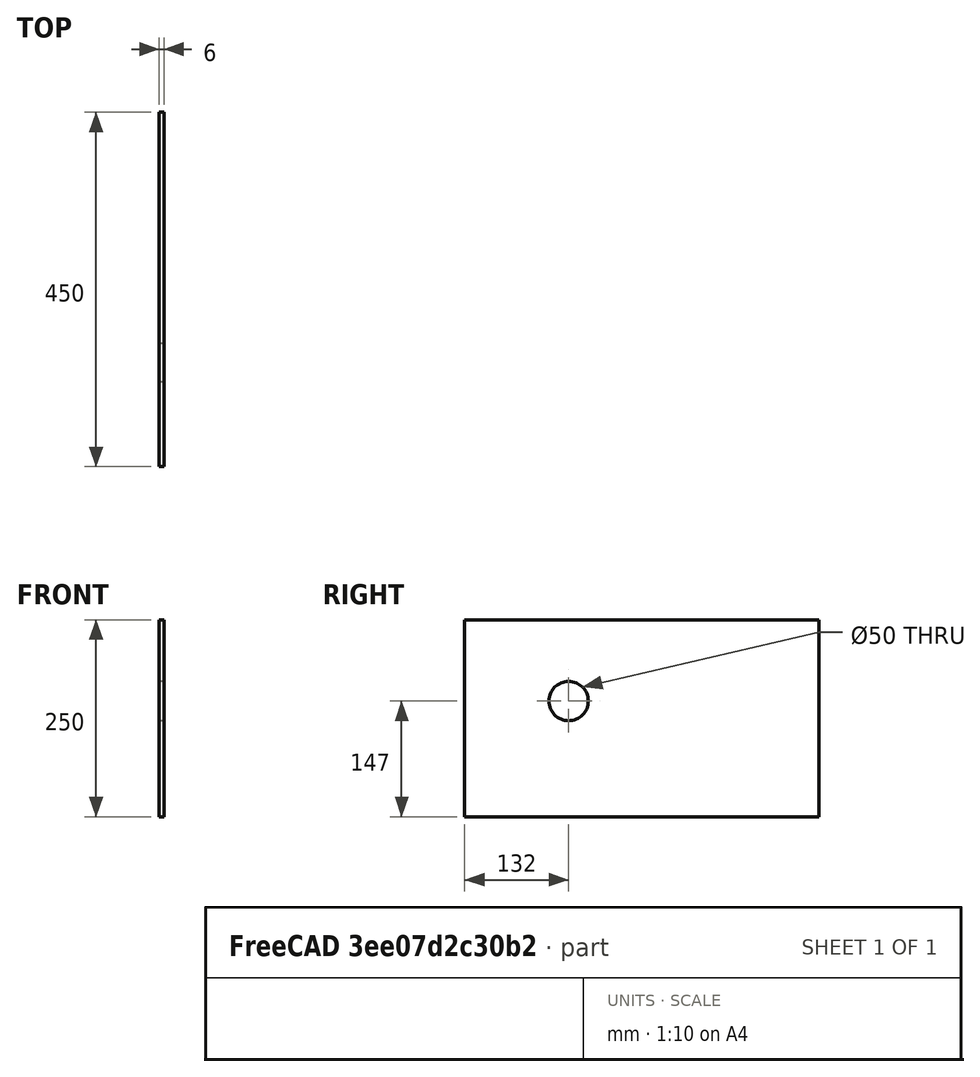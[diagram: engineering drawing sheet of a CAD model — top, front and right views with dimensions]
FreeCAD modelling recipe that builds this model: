
FCSTD DOCUMENT  (FreeCAD 0.18R4 (GitTag))
Label: Gabinete_Lateral2
License: All rights reserved
LicenseURL: http://en.wikipedia.org/wiki/All_rights_reserved
objects: Sketcher::SketchObject×1, PartDesign::Pad×1, PartDesign::Body×1
note: 4 computed .brp shape members not serialized (recipe doc carries the construction recipe); baked Part::Feature solids carry a one-line shape summary decoded from their .brp

FEATURE [Sketcher::SketchObject] Sketch
  MapMode = 5
  Placement = pos=(0,0,0) rot=(0.57735,0.57735,0.57735;2.0944rad)
  Support = -> [YZ_Plane]
  sketch-geometry (5):
    g0: LineSegment StartX=0 StartY=0 StartZ=0 EndX=450 EndY=0 EndZ=0
    g1: LineSegment StartX=450 StartY=0 StartZ=0 EndX=450 EndY=250 EndZ=0
    g2: LineSegment StartX=450 StartY=250 StartZ=0 EndX=0 EndY=250 EndZ=0
    g3: LineSegment StartX=0 StartY=250 StartZ=0 EndX=0 EndY=0 EndZ=0
    g4: Circle CenterX=132 CenterY=147 CenterZ=0 NormalX=0 NormalY=0 NormalZ=1 AngleXU=0 Radius=25
  constraints (14):
    c: Coincident(g0,g1)
    c: Coincident(g1,g2)
    c: Coincident(g2,g3)
    c: Coincident(g3,g0)
    c: Horizontal(g0)
    c: Horizontal(g2)
    c: Vertical(g1)
    c: Vertical(g3)
    c: Coincident(g0,g-1)
    c: DistanceX(g0,g0) = 450
    c: DistanceY(g3,g3) = 250
    c: Radius(g4) = 25
    c: Distance(g4,g0) = 147
    c: Distance(g4,g3) = 132
FEATURE [PartDesign::Pad] Pad
  Length = 6
  Length2 = 100
  Placement = pos=(0,0,0) rot=(0.57735,0.57735,0.57735;2.0944rad)
  Profile = -> Sketch
  Type = 0
FEATURE [PartDesign::Body] Body
  Group = -> [Sketch,Pad]
  Origin = -> Origin
  Tip = -> Pad
